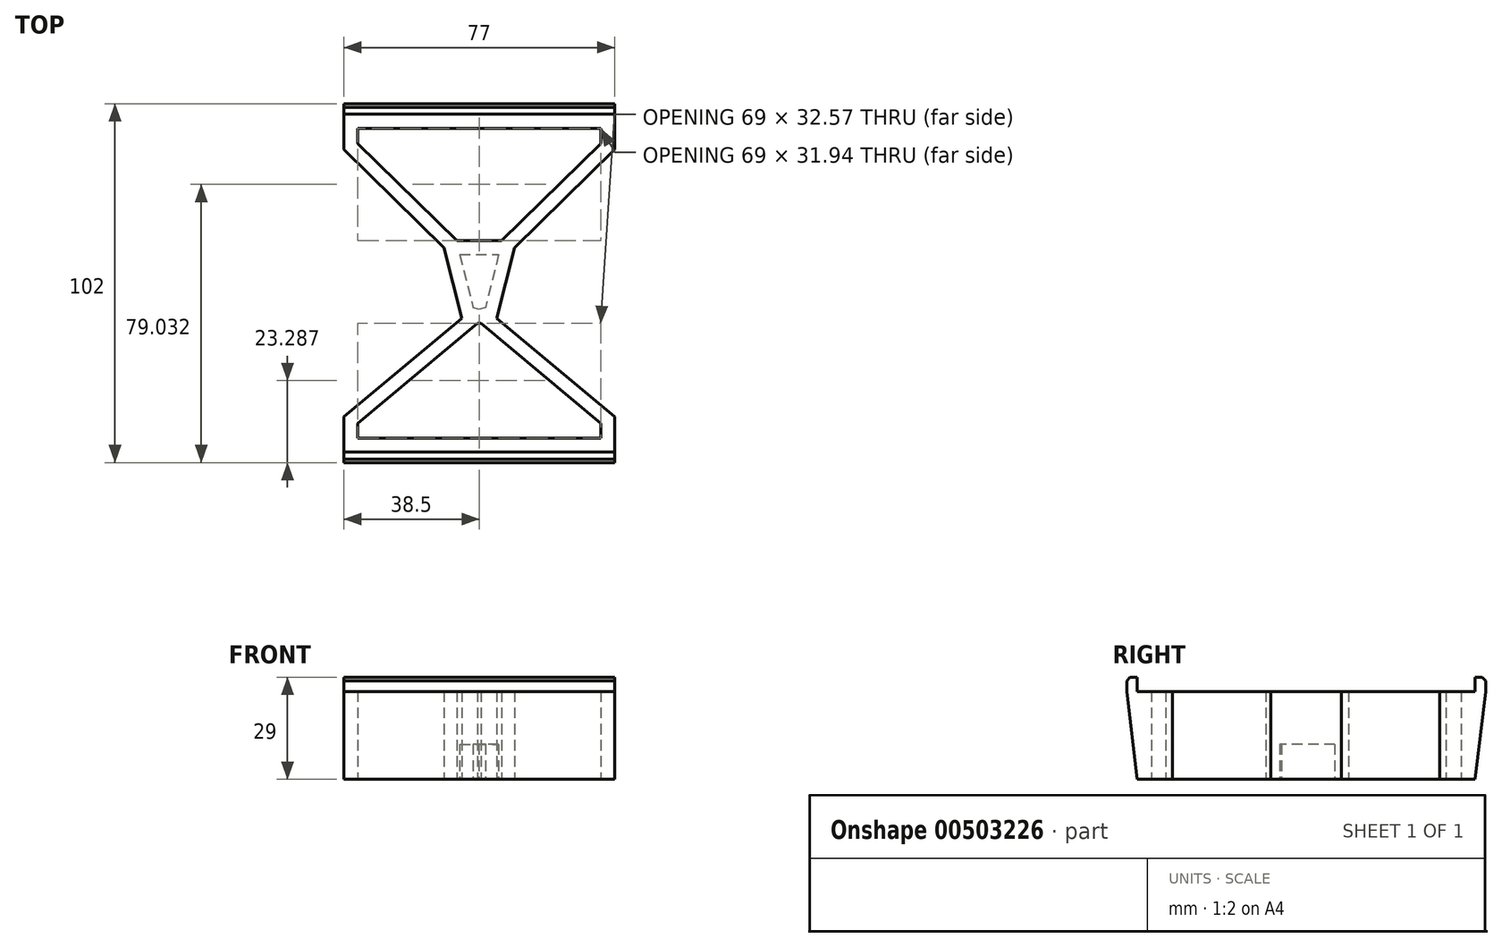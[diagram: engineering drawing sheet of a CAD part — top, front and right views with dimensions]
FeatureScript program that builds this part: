
annotation { "Feature Type Name" : "Feature", "Feature Type Description" : "" }
export const myFeature = defineFeature(function(context is Context, id is Id, definition is map)
    precondition{}
    {
        {
            var Q0;
            Q0=qCreatedBy(makeId("Top.planeOp"),FACE);
            var sketch = newSketch(context, id + "F0", { "sketchPlane" : qUnion([Q0])});
            skLineSegment(sketch, "E0", {"start": v(-38.5, -48) * mm, "end": v(38.5, -48) * mm});
            skLineSegment(sketch, "E1", {"start": v(0, -48) * mm, "end": v(0, 48) * mm, "construction": true});
            skLineSegment(sketch, "E2", {"start": v(-38.5, 48) * mm, "end": v(38.5, 48) * mm});
            skPoint(sketch, "E3", {"position": v(0, 48) * mm});
            skPoint(sketch, "E4", {"position": v(0, 0) * mm});
            skLineSegment(sketch, "E5.0", {"start": v(-38.5, -51) * mm, "end": v(38.5, -51) * mm});
            skLineSegment(sketch, "E6", {"start": v(-38.5, -51) * mm, "end": v(-38.5, -48) * mm});
            skLineSegment(sketch, "E7", {"start": v(38.5, -51) * mm, "end": v(38.5, -48) * mm});
            skLineSegment(sketch, "E8.0", {"start": v(-38.5, 51) * mm, "end": v(38.5, 51) * mm});
            skLineSegment(sketch, "E9", {"start": v(-38.5, 51) * mm, "end": v(-38.5, 48) * mm});
            skLineSegment(sketch, "E10", {"start": v(38.5, 51) * mm, "end": v(38.5, 48) * mm});
            skLineSegment(sketch, "E11", {"start": v(-38.5, -48) * mm, "end": v(-38.5, -38) * mm});
            skLineSegment(sketch, "E12", {"start": v(0, 0) * mm, "end": v(0, -10) * mm, "construction": true});
            skLineSegment(sketch, "E13", {"start": v(0, -10) * mm, "end": v(-5, -10) * mm, "construction": true});
            skLineSegment(sketch, "E14", {"start": v(-5, -10) * mm, "end": v(-38.5, -38) * mm});
            skLineSegment(sketch, "E15", {"start": v(-38.5, 48) * mm, "end": v(-38.5, 38) * mm});
            skLineSegment(sketch, "E16", {"start": v(0, 0) * mm, "end": v(0, 10) * mm, "construction": true});
            skLineSegment(sketch, "E17", {"start": v(0, 10) * mm, "end": v(-10, 10) * mm, "construction": true});
            skLineSegment(sketch, "E18", {"start": v(-10, 10) * mm, "end": v(-38.5, 38) * mm});
            skLineSegment(sketch, "E19", {"start": v(-10, 10) * mm, "end": v(-5, -10) * mm});
            skLineSegment(sketch, "E20.MirrorCS", {"start": v(38.5, 48) * mm, "end": v(38.5, 38) * mm});
            skLineSegment(sketch, "E21.MirrorCS", {"start": v(10, 10) * mm, "end": v(38.5, 38) * mm});
            skLineSegment(sketch, "E22.MirrorCS", {"start": v(10, 10) * mm, "end": v(5, -10) * mm});
            skLineSegment(sketch, "E23.MirrorCS", {"start": v(5, -10) * mm, "end": v(38.5, -38) * mm});
            skLineSegment(sketch, "E24.MirrorCS", {"start": v(38.5, -48) * mm, "end": v(38.5, -38) * mm});
            skLineSegment(sketch, "E25.1", {"start": v(0.47, -11.43) * mm, "end": v(34.5, -39.87) * mm});
            skLineSegment(sketch, "E25.2", {"start": v(34.5, -44) * mm, "end": v(34.5, -39.87) * mm});
            skLineSegment(sketch, "E25.3", {"start": v(-34.5, -44) * mm, "end": v(34.5, -44) * mm});
            skLineSegment(sketch, "E25.4", {"start": v(-34.5, -44) * mm, "end": v(-34.5, -39.87) * mm});
            skLineSegment(sketch, "E25.6", {"start": v(-0.51, -11.46) * mm, "end": v(-34.5, -39.87) * mm});
            skLineSegment(sketch, "E25.7", {"start": v(6.4, 12.06) * mm, "end": v(34.5, 39.68) * mm});
            skLineSegment(sketch, "E25.8", {"start": v(34.5, 44) * mm, "end": v(34.5, 39.68) * mm});
            skLineSegment(sketch, "E25.9", {"start": v(-34.5, 44) * mm, "end": v(34.5, 44) * mm});
            skLineSegment(sketch, "E25.10", {"start": v(-34.5, 44) * mm, "end": v(-34.5, 39.68) * mm});
            skLineSegment(sketch, "E25.11", {"start": v(-6.4, 12.06) * mm, "end": v(-34.5, 39.68) * mm});
            skLineSegment(sketch, "E26", {"start": v(-6.4, 12.06) * mm, "end": v(6.4, 12.06) * mm});
            skLineSegment(sketch, "E27", {"start": v(-0.51, -11.46) * mm, "end": v(0.47, -11.43) * mm});
            skLineSegment(sketch, "E28", {"start": v(5, -10) * mm, "end": v(0.47, -11.43) * mm});
            skLineSegment(sketch, "E29", {"start": v(-0.51, -11.46) * mm, "end": v(-5, -10) * mm});
            skLineSegment(sketch, "E30", {"start": v(-6.4, 12.06) * mm, "end": v(-10, 10) * mm});
            skLineSegment(sketch, "E31", {"start": v(6.4, 12.06) * mm, "end": v(10, 10) * mm});
            skLineSegment(sketch, "E32.0", {"start": v(1.75, -6.94) * mm, "end": v(-0.07, -7.5) * mm});
            skLineSegment(sketch, "E32.1", {"start": v(5.52, 8.16) * mm, "end": v(1.75, -6.94) * mm});
            skLineSegment(sketch, "E32.2", {"start": v(-0.07, -7.5) * mm, "end": v(-1.74, -6.96) * mm});
            skLineSegment(sketch, "E32.3", {"start": v(-5.52, 8.16) * mm, "end": v(-1.74, -6.96) * mm});
            skLineSegment(sketch, "E32.4", {"start": v(-5.52, 8.16) * mm, "end": v(5.52, 8.16) * mm});
            skSolve(sketch);
        }
        {
            var Q0;
            Q0=makeQuery(id+"F0.imprint","IMPRINT",FACE,{"disambiguationData":[TD([[makeQuery(id+"F0.imprint","IMPRINT",EDGE,{"derivedFrom":sQuery(id+"F0.wireOp",EDGE,"E0")}),1.0]])]});
            var Q1;
            Q1=makeQuery(id+"F0.imprint","IMPRINT",FACE,{"disambiguationData":[TD([[makeQuery(id+"F0.imprint","IMPRINT",EDGE,{"derivedFrom":sQuery(id+"F0.wireOp",EDGE,"E19")}),1.0]])]});
            var Q2;
            Q2=makeQuery(id+"F0.imprint","IMPRINT",FACE,{"disambiguationData":[TD([[makeQuery(id+"F0.imprint","IMPRINT",EDGE,{"derivedFrom":sQuery(id+"F0.wireOp",EDGE,"E2")}),-1.0]])]});
            var Q3;
            Q3=makeQuery(id+"F0.imprint","IMPRINT",FACE,{"disambiguationData":[TD([[makeQuery(id+"F0.imprint","IMPRINT",EDGE,{"derivedFrom":sQuery(id+"F0.wireOp",EDGE,"E32.0")}),-1.0]])]});
            extrude(context, id + "F1", {"entities" : qUnion([Q0, Q1, Q2, Q3]), "depth" : 25 * mm});
        }
        {
            var Q0;
            Q0=makeQuery(id+"F0.imprint","IMPRINT",FACE,{"disambiguationData":[TD([[makeQuery(id+"F0.imprint","IMPRINT",EDGE,{"derivedFrom":sQuery(id+"F0.wireOp",EDGE,"E32.0")}),-1.0]])]});
            extrude(context, id + "F2", {"entities" : qUnion([Q0]), "operationType" : NewBodyOperationType.REMOVE, "depth" : 10 * mm});
        }
        {
            var Q0;
            Q0=makeQuery(id+"F0.imprint","IMPRINT",FACE,{"disambiguationData":[TD([[makeQuery(id+"F0.imprint","IMPRINT",EDGE,{"derivedFrom":sQuery(id+"F0.wireOp",EDGE,"E0")}),-1.0]])]});
            var Q1;
            Q1=makeQuery(id+"F0.imprint","IMPRINT",FACE,{"disambiguationData":[TD([[makeQuery(id+"F0.imprint","IMPRINT",EDGE,{"derivedFrom":sQuery(id+"F0.wireOp",EDGE,"E2")}),1.0]])]});
            extrude(context, id + "F3", {"entities" : qUnion([Q0, Q1]), "operationType" : NewBodyOperationType.ADD, "depth" : 29 * mm});
        }
        {
            var Q0;
            Q0=makeQuery(id+"F3.opExtrude","CAP_EDGE",EDGE,{"disambiguationData":[OSD([sQuery(id+"F0.wireOp",EDGE,"E5.0")])],"isStart":true});
            var Q1;
            Q1=makeQuery(id+"F3.opExtrude","CAP_EDGE",EDGE,{"disambiguationData":[OSD([sQuery(id+"F0.wireOp",EDGE,"E8.0")])],"isStart":true});
            chamfer(context, id + "F4", {"entities" : qUnion([Q0, Q1]), "chamferType" : ChamferType.TWO_OFFSETS, "width1" : 25 * mm, "oppositeDirection" : false, "width2" : 3 * mm, "tangentPropagation" : true});
        }
        {
            var Q0;
            Q0=makeQuery(id+"F3.opExtrude","CAP_EDGE",EDGE,{"disambiguationData":[OSD([sQuery(id+"F0.wireOp",EDGE,"E5.0")])],"isStart":false});
            var Q1;
            Q1=makeQuery(id+"F3.opExtrude","CAP_EDGE",EDGE,{"disambiguationData":[OSD([sQuery(id+"F0.wireOp",EDGE,"E8.0")])],"isStart":false});
            chamfer(context, id + "F5", {"entities" : qUnion([Q0, Q1]), "width" : 1 * mm, "tangentPropagation" : true});
        }
    });
